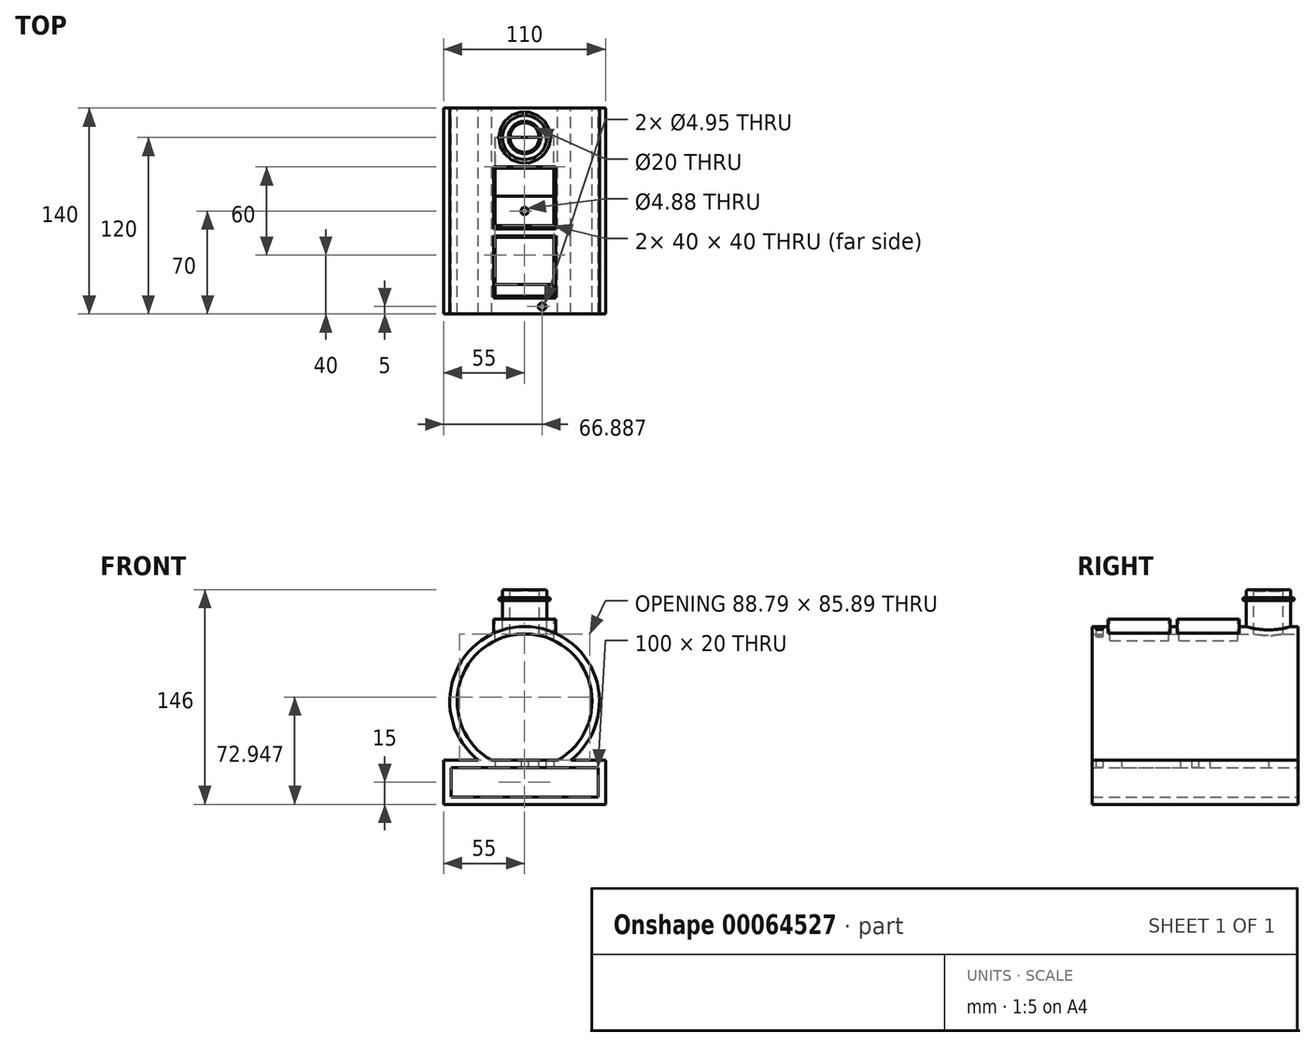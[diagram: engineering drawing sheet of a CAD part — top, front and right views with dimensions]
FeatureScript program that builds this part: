
annotation { "Feature Type Name" : "Feature", "Feature Type Description" : "" }
export const myFeature = defineFeature(function(context is Context, id is Id, definition is map)
    precondition{}
    {
        {
            var Q0;
            Q0=qCreatedBy(makeId("Front.planeOp"),FACE);
            var sketch = newSketch(context, id + "F0", { "sketchPlane" : qUnion([Q0])});
            skCircle(sketch, "E0", {"center": v(0, 0) * mm, "radius": 45.9 * mm});
            skLineSegment(sketch, "E1", {"start": v(-22.5, -40) * mm, "end": v(22.5, -40) * mm});
            skPoint(sketch, "E2", {"position": v(0, -40) * mm});
            skCircle(sketch, "E3", {"center": v(0, 0) * mm, "radius": 50.9 * mm});
            skLineSegment(sketch, "E4", {"start": v(-55, -40) * mm, "end": v(-22.5, -40) * mm});
            skLineSegment(sketch, "E5", {"start": v(0, -40) * mm, "end": v(22.5, -40) * mm});
            skLineSegment(sketch, "E6", {"start": v(22.5, -40) * mm, "end": v(55, -40) * mm});
            skLineSegment(sketch, "E7", {"start": v(55, -40) * mm, "end": v(55, -70) * mm});
            skLineSegment(sketch, "E8", {"start": v(55, -70) * mm, "end": v(-55, -70) * mm});
            skLineSegment(sketch, "E9", {"start": v(-55, -70) * mm, "end": v(-55, -40) * mm});
            skPoint(sketch, "E10", {"position": v(0, -54.83) * mm});
            skPoint(sketch, "E11", {"position": v(0, -45.9) * mm});
            skPoint(sketch, "E12", {"position": v(0, -50.9) * mm});
            skPoint(sketch, "E13", {"position": v(7.73, -70) * mm});
            skLineSegment(sketch, "E14", {"start": v(-50.9, 0) * mm, "end": v(-45.9, 0) * mm});
            skLineSegment(sketch, "E15", {"start": v(-45.9, 0) * mm, "end": v(-17, 0) * mm});
            skLineSegment(sketch, "E16", {"start": v(-17, 0) * mm, "end": v(0, 0) * mm});
            skLineSegment(sketch, "E17", {"start": v(0, 0) * mm, "end": v(17, 0) * mm});
            skLineSegment(sketch, "E18", {"start": v(17, 0) * mm, "end": v(45.9, 0) * mm});
            skLineSegment(sketch, "E19", {"start": v(45.9, 0) * mm, "end": v(50.9, 0) * mm});
            skCircle(sketch, "E20", {"center": v(0, 0) * mm, "radius": 40 * mm});
            skLineSegment(sketch, "E21.bottom", {"start": v(50, -45) * mm, "end": v(-50, -45) * mm});
            skLineSegment(sketch, "E21.top", {"start": v(50, -65) * mm, "end": v(-50, -65) * mm});
            skLineSegment(sketch, "E21.left", {"start": v(50, -45) * mm, "end": v(50, -65) * mm});
            skLineSegment(sketch, "E21.right", {"start": v(-50, -45) * mm, "end": v(-50, -65) * mm});
            skLineSegment(sketch, "E22", {"start": v(-50, -40) * mm, "end": v(-50, -45) * mm, "construction": true});
            skLineSegment(sketch, "E23", {"start": v(-50, -45) * mm, "end": v(-55, -45) * mm, "construction": true});
            skLineSegment(sketch, "E24", {"start": v(55, -45) * mm, "end": v(50, -45) * mm, "construction": true});
            skLineSegment(sketch, "E25", {"start": v(50, -45) * mm, "end": v(50, -40) * mm, "construction": true});
            skPoint(sketch, "E26", {"position": v(0, 40) * mm});
            skPoint(sketch, "E27", {"position": v(0, 45.9) * mm});
            skPoint(sketch, "E28", {"position": v(0, 50.9) * mm});
            skLineSegment(sketch, "E29", {"start": v(-50, -65) * mm, "end": v(-55, -65) * mm});
            skLineSegment(sketch, "E30", {"start": v(-50, -65) * mm, "end": v(-50, -70) * mm});
            skSolve(sketch);
        }
        {
            var Q0;
            {var subQ3=sQuery(id+"F0.wireOp",EDGE,"E14");Q0=makeQuery(id+"F0.imprint","IMPRINT",FACE,{"disambiguationData":[TD([[makeQuery(id+"F0.imprint","IMPRINT",EDGE,{"derivedFrom":subQ3}),-1.0]])]});}
            var Q1;
            {var subQ0=sQuery(id+"F0.wireOp",EDGE,"E4");var subQ5=sQuery(id+"F0.wireOp",EDGE,"E3");var subQ6=makeQuery(id+"F0.imprint","INTERSECT",VERTEX,{"derivedFrom":[subQ5,subQ0]});Q1=makeQuery(id+"F0.imprint","IMPRINT",FACE,{"disambiguationData":[TD([[makeQuery(id+"F0.imprint","IMPRINT",EDGE,{"disambiguationData":[TD([[subQ6,-1.0]])],"derivedFrom":subQ5}),1.0]])]});}
            var Q2;
            {var subQ0=sQuery(id+"F0.wireOp",EDGE,"E14");Q2=makeQuery(id+"F0.imprint","IMPRINT",FACE,{"disambiguationData":[TD([[makeQuery(id+"F0.imprint","IMPRINT",EDGE,{"derivedFrom":subQ0}),1.0]])]});}
            var Q3;
            {var subQ3=sQuery(id+"F0.wireOp",EDGE,"E19");Q3=makeQuery(id+"F0.imprint","IMPRINT",FACE,{"disambiguationData":[TD([[makeQuery(id+"F0.imprint","IMPRINT",EDGE,{"derivedFrom":subQ3}),-1.0]])]});}
            var Q4;
            {var subQ4=sQuery(id+"F0.wireOp",EDGE,"E29");Q4=makeQuery(id+"F0.imprint","IMPRINT",FACE,{"disambiguationData":[TD([[makeQuery(id+"F0.imprint","IMPRINT",EDGE,{"derivedFrom":subQ4}),1.0]])]});}
            var Q5;
            {var subQ0=sQuery(id+"F0.wireOp",EDGE,"E21.right");Q5=makeQuery(id+"F0.imprint","IMPRINT",FACE,{"disambiguationData":[TD([[makeQuery(id+"F0.imprint","IMPRINT",EDGE,{"derivedFrom":subQ0}),-1.0]])]});}
            var Q6;
            {var subQ1=sQuery(id+"F0.wireOp",EDGE,"E7");Q6=makeQuery(id+"F0.imprint","IMPRINT",FACE,{"disambiguationData":[TD([[makeQuery(id+"F0.imprint","IMPRINT",EDGE,{"derivedFrom":subQ1}),-1.0]])]});}
            var Q7;
            {var subQ1=sQuery(id+"F0.wireOp",EDGE,"E1");Q7=makeQuery(id+"F0.imprint","IMPRINT",FACE,{"disambiguationData":[TD([[makeQuery(id+"F0.imprint","IMPRINT",EDGE,{"derivedFrom":subQ1}),-1.0]])]});}
            var Q8;
            {var subQ0=sQuery(id+"F0.wireOp",EDGE,"E6");var subQ5=sQuery(id+"F0.wireOp",EDGE,"E3");var subQ7=makeQuery(id+"F0.imprint","INTERSECT",VERTEX,{"derivedFrom":[subQ5,subQ0]});Q8=makeQuery(id+"F0.imprint","IMPRINT",FACE,{"disambiguationData":[TD([[makeQuery(id+"F0.imprint","IMPRINT",EDGE,{"disambiguationData":[TD([[subQ7,1.0]])],"derivedFrom":subQ5}),1.0]])]});}
            extrude(context, id + "F1", {"entities" : qUnion([Q0, Q1, Q2, Q3, Q4, Q5, Q6, Q7, Q8]), "depth" : 140 * mm});
        }
        {
            var Q0;
            Q0=qCreatedBy(makeId("Top.planeOp"),FACE);
            var Q1;
            Q1=sQuery(id+"F0.wireOp",VERTEX,"E27");
            cPlane(context, id + "F2", {"entities" : qUnion([Q0, Q1]), "cplaneType" : CPlaneType.PLANE_POINT, "offset" : 50 * mm, "width" : 150 * mm, "height" : 150 * mm});
        }
        {
            var Q0;
            Q0=qCreatedBy(makeId("Top.planeOp"),FACE);
            cPlane(context, id + "F3", {"entities" : qUnion([Q0]), "cplaneType" : CPlaneType.OFFSET, "offset" : 56 * mm, "width" : 150 * mm, "height" : 150 * mm});
        }
        {
            var Q0;
            Q0=qCreatedBy(id+"F3.planeOp",FACE);
            cPlane(context, id + "F4", {"entities" : qUnion([Q0]), "cplaneType" : CPlaneType.OFFSET, "offset" : 20 * mm, "width" : 150 * mm, "height" : 150 * mm});
        }
        {
            var Q0;
            Q0=qCreatedBy(id+"F4.planeOp",FACE);
            var sketch = newSketch(context, id + "F5", { "sketchPlane" : qUnion([Q0])});
            skCircle(sketch, "E31", {"center": v(0, -20) * mm, "radius": 10 * mm});
            skCircle(sketch, "E32", {"center": v(0, -20) * mm, "radius": 15 * mm});
            skSolve(sketch);
        }
        {
            var Q0;
            Q0=makeQuery(id+"F5.imprint","IMPRINT",FACE,{"disambiguationData":[TD([[makeQuery(id+"F5.imprint","IMPRINT",EDGE,{"derivedFrom":sQuery(id+"F5.wireOp",EDGE,"E31")}),-1.0]])]});
            extrude(context, id + "F6", {"entities" : qUnion([Q0]), "operationType" : NewBodyOperationType.ADD, "oppositeDirection" : true, "depth" : 30 * mm});
        }
        {
            var Q0;
            Q0=qCreatedBy(id+"F3.planeOp",FACE);
            var sketch = newSketch(context, id + "F7", { "sketchPlane" : qUnion([Q0])});
            skLineSegment(sketch, "E33.bottom", {"start": v(-50, 0) * mm, "end": v(50, 0) * mm});
            skLineSegment(sketch, "E33.top", {"start": v(-50, -140) * mm, "end": v(50, -140) * mm});
            skLineSegment(sketch, "E33.left", {"start": v(-50, 0) * mm, "end": v(-50, -140) * mm});
            skLineSegment(sketch, "E33.right", {"start": v(50, 0) * mm, "end": v(50, -140) * mm});
            skLineSegment(sketch, "E34.bottom", {"start": v(-21, -40) * mm, "end": v(21, -40) * mm});
            skLineSegment(sketch, "E34.top", {"start": v(-21, -82) * mm, "end": v(21, -82) * mm});
            skLineSegment(sketch, "E34.left", {"start": v(-21, -40) * mm, "end": v(-21, -82) * mm});
            skLineSegment(sketch, "E34.right", {"start": v(21, -40) * mm, "end": v(21, -82) * mm});
            skLineSegment(sketch, "E35.bottom", {"start": v(-21, -87) * mm, "end": v(21, -87) * mm});
            skLineSegment(sketch, "E35.top", {"start": v(-21, -129) * mm, "end": v(21, -129) * mm});
            skLineSegment(sketch, "E35.left", {"start": v(-21, -87) * mm, "end": v(-21, -129) * mm});
            skLineSegment(sketch, "E35.right", {"start": v(21, -87) * mm, "end": v(21, -129) * mm});
            skLineSegment(sketch, "E36.bottom", {"start": v(-20, -41) * mm, "end": v(20, -41) * mm});
            skLineSegment(sketch, "E36.top", {"start": v(-20, -81) * mm, "end": v(20, -81) * mm});
            skLineSegment(sketch, "E36.left", {"start": v(-20, -41) * mm, "end": v(-20, -81) * mm});
            skLineSegment(sketch, "E36.right", {"start": v(20, -41) * mm, "end": v(20, -81) * mm});
            skLineSegment(sketch, "E37.bottom", {"start": v(-20, -88) * mm, "end": v(20, -88) * mm});
            skLineSegment(sketch, "E37.top", {"start": v(-20, -128) * mm, "end": v(20, -128) * mm});
            skLineSegment(sketch, "E37.left", {"start": v(-20, -88) * mm, "end": v(-20, -128) * mm});
            skLineSegment(sketch, "E37.right", {"start": v(20, -88) * mm, "end": v(20, -128) * mm});
            skCircle(sketch, "E38", {"center": v(0, -20) * mm, "radius": 15 * mm});
            skCircle(sketch, "E39", {"center": v(0, -20) * mm, "radius": 10 * mm});
            skLineSegment(sketch, "E40", {"start": v(0, -35) * mm, "end": v(0, -40) * mm, "construction": true});
            skLineSegment(sketch, "E41", {"start": v(0, -5) * mm, "end": v(0, 0) * mm, "construction": true});
            skSolve(sketch);
        }
        {
            var Q0;
            Q0=makeQuery(id+"F7.imprint","IMPRINT",FACE,{"disambiguationData":[TD([[makeQuery(id+"F7.imprint","IMPRINT",EDGE,{"derivedFrom":sQuery(id+"F7.wireOp",EDGE,"E39")}),1.0]])]});
            extrude(context, id + "F8", {"entities" : qUnion([Q0]), "operationType" : NewBodyOperationType.REMOVE, "oppositeDirection" : true, "depth" : 25 * mm});
        }
        {
            var Q0;
            Q0=makeQuery(id+"F7.imprint","IMPRINT",FACE,{"disambiguationData":[TD([[makeQuery(id+"F7.imprint","IMPRINT",EDGE,{"derivedFrom":sQuery(id+"F7.wireOp",EDGE,"E34.bottom")}),-1.0]])]});
            var Q1;
            Q1=makeQuery(id+"F7.imprint","IMPRINT",FACE,{"disambiguationData":[TD([[makeQuery(id+"F7.imprint","IMPRINT",EDGE,{"derivedFrom":sQuery(id+"F7.wireOp",EDGE,"E35.bottom")}),-1.0]])]});
            extrude(context, id + "F9", {"entities" : qUnion([Q0, Q1]), "operationType" : NewBodyOperationType.ADD, "oppositeDirection" : true, "depth" : 10 * mm});
        }
        {
            var Q0;
            Q0=makeQuery(id+"F7.imprint","IMPRINT",FACE,{"disambiguationData":[TD([[makeQuery(id+"F7.imprint","IMPRINT",EDGE,{"derivedFrom":sQuery(id+"F7.wireOp",EDGE,"E36.bottom")}),-1.0]])]});
            var Q1;
            Q1=makeQuery(id+"F7.imprint","IMPRINT",FACE,{"disambiguationData":[TD([[makeQuery(id+"F7.imprint","IMPRINT",EDGE,{"derivedFrom":sQuery(id+"F7.wireOp",EDGE,"E37.bottom")}),-1.0]])]});
            extrude(context, id + "F10", {"entities" : qUnion([Q0, Q1]), "operationType" : NewBodyOperationType.REMOVE, "oppositeDirection" : true, "depth" : 25 * mm});
        }
        {
            var Q0;
            Q0=makeQuery(id+"F1.opExtrude","SWEPT_FACE",FACE,{"disambiguationData":[OSD([sQuery(id+"F0.wireOp",EDGE,"E21.bottom")])]});
            var sketch = newSketch(context, id + "F11", { "sketchPlane" : qUnion([Q0])});
            skLineSegment(sketch, "E42.bottom", {"start": v(-20, 60) * mm, "end": v(20, 60) * mm});
            skLineSegment(sketch, "E42.top", {"start": v(-20, 20) * mm, "end": v(20, 20) * mm});
            skLineSegment(sketch, "E42.left", {"start": v(-20, 60) * mm, "end": v(-20, 20) * mm});
            skLineSegment(sketch, "E42.right", {"start": v(20, 60) * mm, "end": v(20, 20) * mm});
            skLineSegment(sketch, "E43.bottom", {"start": v(-20, 120) * mm, "end": v(20, 120) * mm});
            skLineSegment(sketch, "E43.top", {"start": v(-20, 80) * mm, "end": v(20, 80) * mm});
            skLineSegment(sketch, "E43.left", {"start": v(-20, 120) * mm, "end": v(-20, 80) * mm});
            skLineSegment(sketch, "E43.right", {"start": v(20, 120) * mm, "end": v(20, 80) * mm});
            skCircle(sketch, "E44", {"center": v(0, 70) * mm, "radius": 2.44 * mm});
            skCircle(sketch, "E45", {"center": v(11.89, 135) * mm, "radius": 2.48 * mm});
            skLineSegment(sketch, "E46", {"start": v(0, 70) * mm, "end": v(0, 140) * mm, "construction": true});
            skLineSegment(sketch, "E47", {"start": v(11.89, 135) * mm, "end": v(0, 135) * mm, "construction": true});
            skLineSegment(sketch, "E48", {"start": v(0, 135) * mm, "end": v(11.89, 135) * mm, "construction": true});
            skLineSegment(sketch, "E49", {"start": v(11.89, 135) * mm, "end": v(23.77, 135) * mm, "construction": true});
            skLineSegment(sketch, "E50", {"start": v(-20, 80) * mm, "end": v(-23.77, 80) * mm, "construction": true});
            skLineSegment(sketch, "E51", {"start": v(20, 80) * mm, "end": v(23.77, 80) * mm, "construction": true});
            skSolve(sketch);
        }
        {
            var Q0;
            Q0 = qSketchRegion(id + "F11", true);
            extrude(context, id + "F12", {"entities" : qUnion([Q0]), "operationType" : NewBodyOperationType.REMOVE, "oppositeDirection" : true, "depth" : 25 * mm});
        }
        {
            var Q0;
            Q0=makeQuery(id+"F11.imprint","IMPRINT",FACE,{"disambiguationData":[TD([[makeQuery(id+"F11.imprint","IMPRINT",EDGE,{"derivedFrom":sQuery(id+"F11.wireOp",EDGE,"E45")}),1.0]])]});
            extrude(context, id + "F13", {"entities" : qUnion([Q0]), "operationType" : NewBodyOperationType.REMOVE, "oppositeDirection" : true, "depth" : 100 * mm});
        }
        {
            var Q0;
            Q0=qCreatedBy(id+"F4.planeOp",FACE);
            cPlane(context, id + "F14", {"entities" : qUnion([Q0]), "cplaneType" : CPlaneType.OFFSET, "offset" : 7.5 * mm, "oppositeDirection" : true, "width" : 150 * mm, "height" : 150 * mm});
        }
        {
            var Q0;
            Q0=qCreatedBy(id+"F14.planeOp",FACE);
            var sketch = newSketch(context, id + "F15", { "sketchPlane" : qUnion([Q0])});
            skCircle(sketch, "E52", {"center": v(0, -20) * mm, "radius": 17.5 * mm});
            skCircle(sketch, "E53", {"center": v(0, -20) * mm, "radius": 10 * mm});
            skSolve(sketch);
        }
        {
            var Q0;
            Q0=makeQuery(id+"F15.imprint","IMPRINT",FACE,{"disambiguationData":[TD([[makeQuery(id+"F15.imprint","IMPRINT",EDGE,{"derivedFrom":sQuery(id+"F15.wireOp",EDGE,"E52")}),1.0]])]});
            extrude(context, id + "F16", {"entities" : qUnion([Q0]), "operationType" : NewBodyOperationType.ADD, "depth" : 2 * mm});
        }
        {
            var Q0;
            Q0=makeQuery(id+"F16.opExtrude","CAP_EDGE",EDGE,{"disambiguationData":[OSD([sQuery(id+"F15.wireOp",EDGE,"E52")])],"isStart":false});
            var Q1;
            Q1=makeQuery(id+"F16.opExtrude","CAP_EDGE",EDGE,{"disambiguationData":[OSD([sQuery(id+"F15.wireOp",EDGE,"E52")])],"isStart":true});
            var Q2;
            Q2=makeQuery(id+"F6.opExtrude","CAP_EDGE",EDGE,{"disambiguationData":[OSD([sQuery(id+"F5.wireOp",EDGE,"E32")])],"isStart":true});
            fillet(context, id + "F17", {"entities" : qUnion([Q0, Q1, Q2]), "radius" : 1 * mm, "tangentPropagation" : true, "allowEdgeOverflow" : false});
        }
        {
            var Q0;
            Q0=makeQuery(id+"F6.opExtrude","CAP_EDGE",EDGE,{"disambiguationData":[OSD([sQuery(id+"F5.wireOp",EDGE,"E31")])],"isStart":true});
            chamfer(context, id + "F18", {"entities" : qUnion([Q0]), "width" : 1 * mm, "tangentPropagation" : true});
        }
    });
